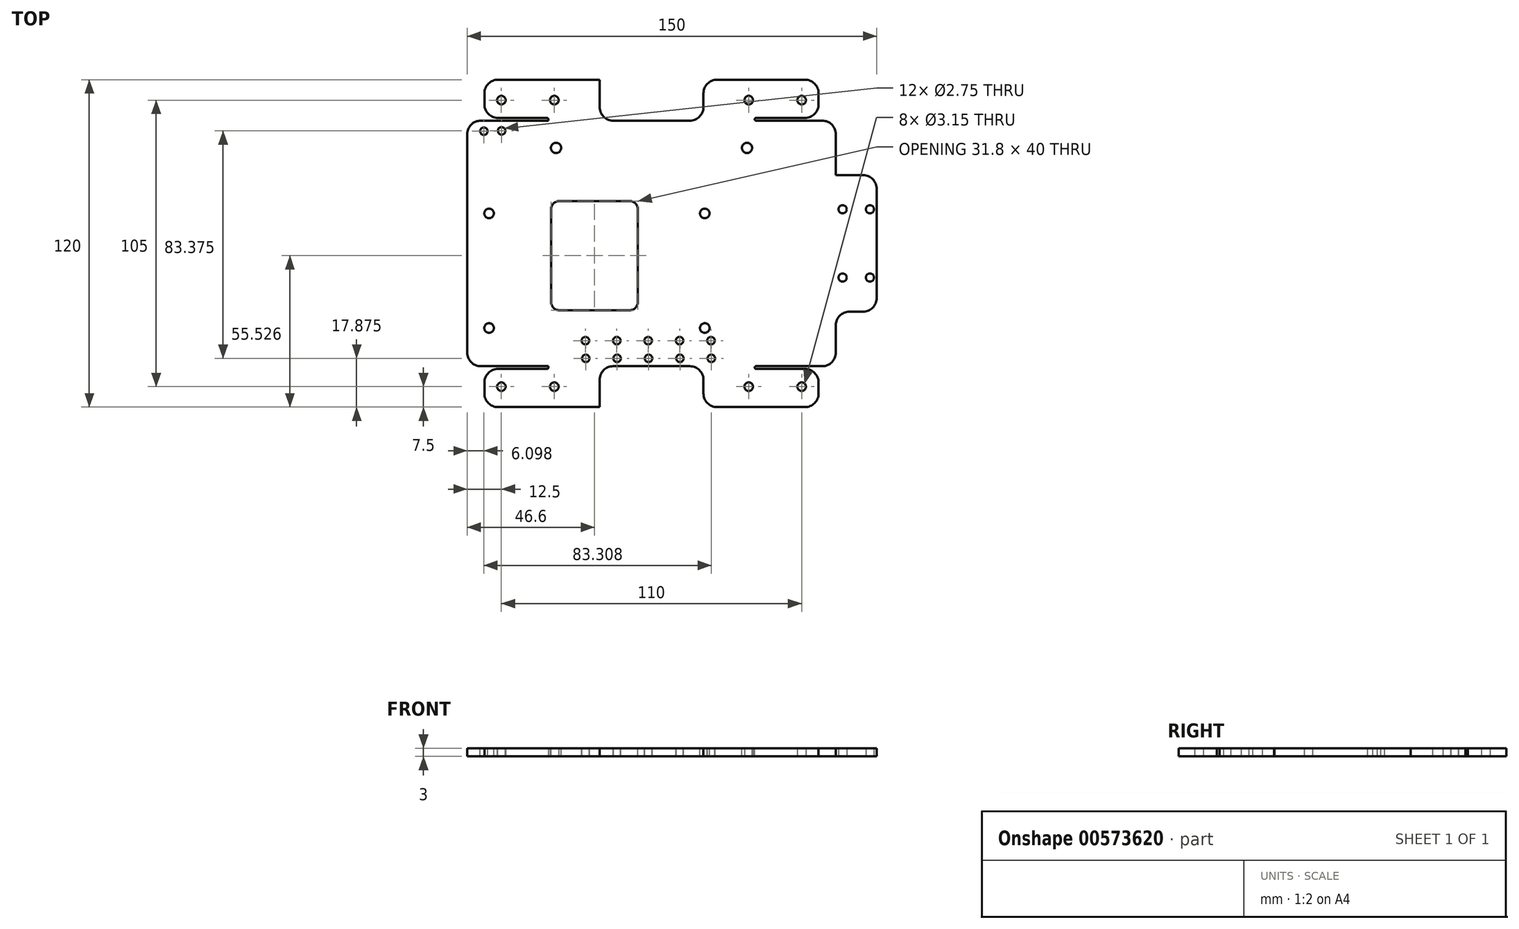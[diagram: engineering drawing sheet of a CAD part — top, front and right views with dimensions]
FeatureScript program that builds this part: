
annotation { "Feature Type Name" : "Feature", "Feature Type Description" : "" }
export const myFeature = defineFeature(function(context is Context, id is Id, definition is map)
    precondition{}
    {
        {
            var Q0;
            Q0=qCreatedBy(makeId("Top.planeOp"),FACE);
            var sketch = newSketch(context, id + "F0", { "sketchPlane" : qUnion([Q0])});
            skLineSegment(sketch, "E0.bottom", {"start": v(67.5, -45) * mm, "end": v(-67.5, -45) * mm});
            skLineSegment(sketch, "E0.top", {"start": v(67.5, 45) * mm, "end": v(-67.5, 45) * mm});
            skLineSegment(sketch, "E0.left", {"start": v(67.5, -45) * mm, "end": v(67.5, 45) * mm});
            skLineSegment(sketch, "E0.right", {"start": v(-67.5, -45) * mm, "end": v(-67.5, 45) * mm});
            skPoint(sketch, "E0.middle", {"position": v(0, 0) * mm});
            skSolve(sketch);
        }
        {
            var Q0;
            Q0 = qSketchRegion(id + "F0", true);
            extrude(context, id + "F1", {"entities" : qUnion([Q0]), "depth" : 3 * mm, "offsetDistance" : 25 * mm});
        }
        {
            var Q0;
            Q0=makeQuery(id+"F1.opExtrude","CAP_FACE",FACE,{"disambiguationData":[OSD([sQuery(id+"F0.wireOp",EDGE,"E0.bottom"),sQuery(id+"F0.wireOp",EDGE,"E0.top"),sQuery(id+"F0.wireOp",EDGE,"E0.left"),sQuery(id+"F0.wireOp",EDGE,"E0.right")])],"isStart":false});
            var sketch = newSketch(context, id + "F2", { "sketchPlane" : qUnion([Q0])});
            skLineSegment(sketch, "E1.bottom", {"start": v(-50.8, 45) * mm, "end": v(-37.8, 45) * mm});
            skLineSegment(sketch, "E1.top", {"start": v(-50.8, -45) * mm, "end": v(-37.8, -45) * mm});
            skLineSegment(sketch, "E1.left", {"start": v(-50.8, 45) * mm, "end": v(-50.8, -45) * mm});
            skLineSegment(sketch, "E1.right", {"start": v(-37.8, 45) * mm, "end": v(-37.8, -45) * mm});
            skLineSegment(sketch, "E2.bottom", {"start": v(37.8, 45) * mm, "end": v(50.8, 45) * mm});
            skLineSegment(sketch, "E2.top", {"start": v(37.8, -45) * mm, "end": v(50.8, -45) * mm});
            skLineSegment(sketch, "E2.left", {"start": v(37.8, 45) * mm, "end": v(37.8, -45) * mm});
            skLineSegment(sketch, "E2.right", {"start": v(50.8, 45) * mm, "end": v(50.8, -45) * mm});
            skLineSegment(sketch, "E3", {"start": v(-37.8, -35.2) * mm, "end": v(37.8, -35.2) * mm, "construction": true});
            skPoint(sketch, "E4", {"position": v(0, -35.2) * mm});
            skLineSegment(sketch, "E5", {"start": v(0, 50.5) * mm, "end": v(0, -49.91) * mm, "construction": true});
            skSolve(sketch);
        }
        {
            var Q0;
            Q0=makeQuery(id+"F1.opExtrude","CAP_FACE",FACE,{"disambiguationData":[OSD([sQuery(id+"F0.wireOp",EDGE,"E0.bottom"),sQuery(id+"F0.wireOp",EDGE,"E0.top"),sQuery(id+"F0.wireOp",EDGE,"E0.left"),sQuery(id+"F0.wireOp",EDGE,"E0.right")])],"isStart":false});
            var sketch = newSketch(context, id + "F3", { "sketchPlane" : qUnion([Q0])});
            skLineSegment(sketch, "E6.bottom", {"start": v(-59.5, 11) * mm, "end": v(19.5, 11) * mm, "construction": true});
            skLineSegment(sketch, "E6.top", {"start": v(-59.5, -31) * mm, "end": v(19.5, -31) * mm, "construction": true});
            skLineSegment(sketch, "E6.left", {"start": v(-59.5, 11) * mm, "end": v(-59.5, -31) * mm, "construction": true});
            skLineSegment(sketch, "E6.right", {"start": v(19.5, 11) * mm, "end": v(19.5, -31) * mm, "construction": true});
            skCircle(sketch, "E7", {"center": v(-59.5, 11) * mm, "radius": 1.75 * mm});
            skCircle(sketch, "E8", {"center": v(19.5, 11) * mm, "radius": 1.75 * mm});
            skCircle(sketch, "E9", {"center": v(19.5, -31) * mm, "radius": 1.75 * mm});
            skCircle(sketch, "E10", {"center": v(-59.5, -31) * mm, "radius": 1.75 * mm});
            skLineSegment(sketch, "E11", {"start": v(-20, 11) * mm, "end": v(-20, -31) * mm, "construction": true});
            skSolve(sketch);
        }
        {
            var Q0;
            Q0 = qSketchRegion(id + "F3", true);
            extrude(context, id + "F4", {"entities" : qUnion([Q0]), "operationType" : NewBodyOperationType.REMOVE, "endBound" : BoundingType.THROUGH_ALL, "oppositeDirection" : true, "depth" : 25 * mm, "offsetDistance" : 25 * mm});
        }
        {
            var Q0;
            Q0=qCreatedBy(makeId("Top.planeOp"),FACE);
            var sketch = newSketch(context, id + "F5", { "sketchPlane" : qUnion([Q0])});
            skLineSegment(sketch, "E12.bottom", {"start": v(-37.8, 45) * mm, "end": v(37.8, 45) * mm});
            skLineSegment(sketch, "E12.top", {"start": v(-37.8, 60) * mm, "end": v(37.8, 60) * mm});
            skLineSegment(sketch, "E12.left", {"start": v(-37.8, 45) * mm, "end": v(-37.8, 46) * mm});
            skLineSegment(sketch, "E12.right", {"start": v(37.8, 45) * mm, "end": v(37.8, 46) * mm});
            skLineSegment(sketch, "E13", {"start": v(0, 42.7) * mm, "end": v(0, -42.57) * mm, "construction": true});
            skLineSegment(sketch, "E14", {"start": v(-65.02, 0) * mm, "end": v(65.15, 0) * mm, "construction": true});
            skCircle(sketch, "E15", {"center": v(-55, 52.5) * mm, "radius": 1.57 * mm});
            skCircle(sketch, "E16", {"center": v(-35.6, 52.5) * mm, "radius": 1.57 * mm});
            skLineSegment(sketch, "E17", {"start": v(-55, 52.5) * mm, "end": v(-35.6, 52.5) * mm, "construction": true});
            skLineSegment(sketch, "E18", {"start": v(-45.3, 60) * mm, "end": v(-45.3, 45) * mm, "construction": true});
            skPoint(sketch, "E19", {"position": v(-45.3, 52.5) * mm});
            skPoint(sketch, "E19.positionSnap0", {"position": v(-45.3, 52.5) * mm});
            skCircle(sketch, "E20", {"center": v(-55, 52.5) * mm, "radius": 2.2 * mm, "construction": true});
            skCircle(sketch, "E21", {"center": v(-35.6, 52.5) * mm, "radius": 2.2 * mm, "construction": true});
            skLineSegment(sketch, "E22.bottom", {"start": v(-37.8, 46) * mm, "end": v(-61.2, 46) * mm});
            skLineSegment(sketch, "E22.top", {"start": v(-37.76, 60) * mm, "end": v(-61.2, 60) * mm});
            skLineSegment(sketch, "E22.right", {"start": v(-61.2, 46) * mm, "end": v(-61.2, 60) * mm});
            skPoint(sketch, "E23.MirrorP", {"position": v(45.3, 52.5) * mm});
            skLineSegment(sketch, "E24.MirrorCS", {"start": v(55, 52.5) * mm, "end": v(35.6, 52.5) * mm, "construction": true});
            skLineSegment(sketch, "E25.MirrorCS", {"start": v(45.3, 60) * mm, "end": v(45.3, 45) * mm, "construction": true});
            skCircle(sketch, "E26.MirrorC", {"center": v(55, 52.5) * mm, "radius": 2.2 * mm, "construction": true});
            skCircle(sketch, "E27.MirrorC", {"center": v(55, 52.5) * mm, "radius": 1.57 * mm});
            skCircle(sketch, "E28.MirrorC", {"center": v(35.6, 52.5) * mm, "radius": 1.57 * mm});
            skCircle(sketch, "E29.MirrorC", {"center": v(35.6, 52.5) * mm, "radius": 2.2 * mm, "construction": true});
            skLineSegment(sketch, "E30.bottom", {"start": v(37.8, 60) * mm, "end": v(61.2, 60) * mm});
            skLineSegment(sketch, "E30.top", {"start": v(37.8, 46) * mm, "end": v(61.2, 46) * mm});
            skLineSegment(sketch, "E30.right", {"start": v(61.2, 60) * mm, "end": v(61.2, 46) * mm});
            skLineSegment(sketch, "E31", {"start": v(-57.2, 52.5) * mm, "end": v(-61.2, 52.5) * mm, "construction": true});
            skLineSegment(sketch, "E32", {"start": v(57.2, 52.5) * mm, "end": v(61.2, 52.5) * mm, "construction": true});
            skLineSegment(sketch, "E33.MirrorCS", {"start": v(37.8, -45) * mm, "end": v(37.8, -46) * mm});
            skLineSegment(sketch, "E34.MirrorCS", {"start": v(-37.8, -45) * mm, "end": v(-37.8, -46) * mm});
            skPoint(sketch, "E35.MirrorP", {"position": v(-45.3, -52.5) * mm});
            skPoint(sketch, "E36.MirrorP", {"position": v(45.3, -52.5) * mm});
            skLineSegment(sketch, "E37.MirrorCS", {"start": v(-57.2, -52.5) * mm, "end": v(-61.2, -52.5) * mm, "construction": true});
            skCircle(sketch, "E38.MirrorC", {"center": v(-35.6, -52.5) * mm, "radius": 2.2 * mm, "construction": true});
            skLineSegment(sketch, "E39.MirrorCS", {"start": v(61.2, -60) * mm, "end": v(61.2, -46) * mm});
            skLineSegment(sketch, "E40.MirrorCS", {"start": v(45.3, -60) * mm, "end": v(45.3, -45) * mm, "construction": true});
            skLineSegment(sketch, "E41.MirrorCS", {"start": v(57.2, -52.5) * mm, "end": v(61.2, -52.5) * mm, "construction": true});
            skCircle(sketch, "E42.MirrorC", {"center": v(-55, -52.5) * mm, "radius": 2.2 * mm, "construction": true});
            skCircle(sketch, "E43.MirrorC", {"center": v(55, -52.5) * mm, "radius": 1.57 * mm});
            skLineSegment(sketch, "E44.MirrorCS", {"start": v(55, -52.5) * mm, "end": v(35.6, -52.5) * mm, "construction": true});
            skLineSegment(sketch, "E45.MirrorCS", {"start": v(-55, -52.5) * mm, "end": v(-35.6, -52.5) * mm, "construction": true});
            skLineSegment(sketch, "E46.MirrorCS", {"start": v(-45.3, -60) * mm, "end": v(-45.3, -45) * mm, "construction": true});
            skCircle(sketch, "E47.MirrorC", {"center": v(35.6, -52.5) * mm, "radius": 1.57 * mm});
            skLineSegment(sketch, "E48.MirrorCS", {"start": v(37.8, -46) * mm, "end": v(61.2, -46) * mm});
            skCircle(sketch, "E49.MirrorC", {"center": v(-35.6, -52.5) * mm, "radius": 1.57 * mm});
            skLineSegment(sketch, "E50.MirrorCS", {"start": v(37.8, -60) * mm, "end": v(61.2, -60) * mm});
            skLineSegment(sketch, "E51.MirrorCS", {"start": v(-37.8, -45) * mm, "end": v(37.8, -45) * mm});
            skCircle(sketch, "E52.MirrorC", {"center": v(55, -52.5) * mm, "radius": 2.2 * mm, "construction": true});
            skLineSegment(sketch, "E53.MirrorCS", {"start": v(-61.2, -46) * mm, "end": v(-61.2, -60) * mm});
            skCircle(sketch, "E54.MirrorC", {"center": v(-55, -52.5) * mm, "radius": 1.57 * mm});
            skLineSegment(sketch, "E55.MirrorCS", {"start": v(-37.76, -60) * mm, "end": v(-61.2, -60) * mm});
            skLineSegment(sketch, "E56.MirrorCS", {"start": v(-37.8, -60) * mm, "end": v(37.8, -60) * mm});
            skCircle(sketch, "E57.MirrorC", {"center": v(35.6, -52.5) * mm, "radius": 2.2 * mm, "construction": true});
            skLineSegment(sketch, "E58.MirrorCS", {"start": v(-37.8, -46) * mm, "end": v(-61.2, -46) * mm});
            skSolve(sketch);
        }
        {
            var Q0;
            Q0 = qSketchRegion(id + "F5", true);
            var Q1;
            Q1=makeQuery(id+"F1.opExtrude","CAP_FACE",FACE,{"disambiguationData":[OSD([sQuery(id+"F0.wireOp",EDGE,"E0.bottom"),sQuery(id+"F0.wireOp",EDGE,"E0.top"),sQuery(id+"F0.wireOp",EDGE,"E0.left"),sQuery(id+"F0.wireOp",EDGE,"E0.right")])],"isStart":false});
            extrude(context, id + "F6", {"entities" : qUnion([Q0]), "operationType" : NewBodyOperationType.ADD, "endBound" : BoundingType.UP_TO_SURFACE, "depth" : 25 * mm, "endBoundEntityFace" : qUnion([Q1]), "offsetDistance" : 25 * mm});
        }
        {
            var Q0;
            {var subQ0=sQuery(id+"F0.wireOp",EDGE,"E0.right");var subQ1=sQuery(id+"F0.wireOp",EDGE,"E0.left");var subQ2=sQuery(id+"F0.wireOp",EDGE,"E0.top");var subQ3=sQuery(id+"F0.wireOp",EDGE,"E0.bottom");Q0=makeQuery(id+"F6.boolean.opBoolean","MERGE",FACE,{"derivedFrom":[makeQuery(id+"F1.opExtrude","CAP_FACE",FACE,{"disambiguationData":[OSD([subQ3,subQ2,subQ1,subQ0])],"isStart":false}),makeQuery(id+"F6.opExtrude","CAP_FACE",FACE,{"disambiguationData":[OSD([subQ3,subQ2,subQ1,subQ0]),OD(0.0)],"isStart":false}),makeQuery(id+"F6.opExtrude","CAP_FACE",FACE,{"disambiguationData":[OSD([subQ3,subQ2,subQ1,subQ0]),OD(1.0)],"isStart":false})]});}
            var sketch = newSketch(context, id + "F7", { "sketchPlane" : qUnion([Q0])});
            skLineSegment(sketch, "E59.bottom", {"start": v(-19.02, -60) * mm, "end": v(19.02, -60) * mm});
            skLineSegment(sketch, "E59.top", {"start": v(-19.02, -45) * mm, "end": v(19.02, -45) * mm});
            skLineSegment(sketch, "E59.left", {"start": v(-19.02, -60) * mm, "end": v(-19.02, -45) * mm});
            skLineSegment(sketch, "E59.right", {"start": v(19.02, -60) * mm, "end": v(19.02, -45) * mm});
            skLineSegment(sketch, "E60", {"start": v(0, -60) * mm, "end": v(0, -45) * mm, "construction": true});
            skLineSegment(sketch, "E61", {"start": v(-67.5, 0) * mm, "end": v(67.5, 0) * mm, "construction": true});
            skLineSegment(sketch, "E62.MirrorCS", {"start": v(-19.02, 45) * mm, "end": v(19.02, 45) * mm});
            skLineSegment(sketch, "E63.MirrorCS", {"start": v(-19.02, 60) * mm, "end": v(19.02, 60) * mm});
            skLineSegment(sketch, "E64.MirrorCS", {"start": v(19.02, 60) * mm, "end": v(19.02, 45) * mm});
            skLineSegment(sketch, "E65.MirrorCS", {"start": v(-19.02, 60) * mm, "end": v(-19.02, 45) * mm});
            skSolve(sketch);
        }
        {
            var Q0;
            Q0 = qSketchRegion(id + "F7", true);
            var Q1;
            Q1=makeQuery(id+"F6.boolean.opBoolean","MERGE",FACE,{"derivedFrom":[makeQuery(id+"F1.opExtrude","CAP_FACE",FACE,{"disambiguationData":[OSD([sQuery(id+"F0.wireOp",EDGE,"E0.bottom"),sQuery(id+"F0.wireOp",EDGE,"E0.top"),sQuery(id+"F0.wireOp",EDGE,"E0.left"),sQuery(id+"F0.wireOp",EDGE,"E0.right")])],"isStart":true}),makeQuery(id+"F6.opExtrude","CAP_FACE",FACE,{"disambiguationData":[OSD([sQuery(id+"F5.wireOp",EDGE,"E12.bottom"),sQuery(id+"F5.wireOp",EDGE,"E12.top"),sQuery(id+"F5.wireOp",EDGE,"E12.left"),sQuery(id+"F5.wireOp",EDGE,"E15"),sQuery(id+"F5.wireOp",EDGE,"E16"),sQuery(id+"F5.wireOp",EDGE,"E22.bottom"),sQuery(id+"F5.wireOp",EDGE,"E22.top"),sQuery(id+"F5.wireOp",EDGE,"E22.right"),sQuery(id+"F5.wireOp",EDGE,"E12.right"),sQuery(id+"F5.wireOp",EDGE,"E27.MirrorC"),sQuery(id+"F5.wireOp",EDGE,"E28.MirrorC"),sQuery(id+"F5.wireOp",EDGE,"E30.bottom"),sQuery(id+"F5.wireOp",EDGE,"E30.top"),sQuery(id+"F5.wireOp",EDGE,"E30.right")])],"isStart":true}),makeQuery(id+"F6.opExtrude","CAP_FACE",FACE,{"disambiguationData":[OSD([sQuery(id+"F5.wireOp",EDGE,"E33.MirrorCS"),sQuery(id+"F5.wireOp",EDGE,"E34.MirrorCS"),sQuery(id+"F5.wireOp",EDGE,"E39.MirrorCS"),sQuery(id+"F5.wireOp",EDGE,"E43.MirrorC"),sQuery(id+"F5.wireOp",EDGE,"E47.MirrorC"),sQuery(id+"F5.wireOp",EDGE,"E48.MirrorCS"),sQuery(id+"F5.wireOp",EDGE,"E49.MirrorC"),sQuery(id+"F5.wireOp",EDGE,"E50.MirrorCS"),sQuery(id+"F5.wireOp",EDGE,"E51.MirrorCS"),sQuery(id+"F5.wireOp",EDGE,"E53.MirrorCS"),sQuery(id+"F5.wireOp",EDGE,"E54.MirrorC"),sQuery(id+"F5.wireOp",EDGE,"E55.MirrorCS"),sQuery(id+"F5.wireOp",EDGE,"E56.MirrorCS"),sQuery(id+"F5.wireOp",EDGE,"E58.MirrorCS")])],"isStart":true})]});
            extrude(context, id + "F8", {"entities" : qUnion([Q0]), "operationType" : NewBodyOperationType.REMOVE, "endBound" : BoundingType.UP_TO_SURFACE, "oppositeDirection" : true, "depth" : 25 * mm, "endBoundEntityFace" : qUnion([Q1]), "offsetDistance" : 25 * mm});
        }
        {
            var Q0;
            {var subQ0=sQuery(id+"F0.wireOp",EDGE,"E0.right");var subQ1=sQuery(id+"F0.wireOp",EDGE,"E0.left");var subQ2=sQuery(id+"F0.wireOp",EDGE,"E0.top");var subQ3=sQuery(id+"F0.wireOp",EDGE,"E0.bottom");Q0=makeQuery(id+"F6.boolean.opBoolean","MERGE",FACE,{"derivedFrom":[makeQuery(id+"F1.opExtrude","CAP_FACE",FACE,{"disambiguationData":[OSD([subQ3,subQ2,subQ1,subQ0])],"isStart":false}),makeQuery(id+"F6.opExtrude","CAP_FACE",FACE,{"disambiguationData":[OSD([subQ3,subQ2,subQ1,subQ0]),OD(0.0)],"isStart":false}),makeQuery(id+"F6.opExtrude","CAP_FACE",FACE,{"disambiguationData":[OSD([subQ3,subQ2,subQ1,subQ0]),OD(1.0)],"isStart":false})]});}
            var sketch = newSketch(context, id + "F9", { "sketchPlane" : qUnion([Q0])});
            skCircle(sketch, "E66", {"center": v(-61.4, 41.12) * mm, "radius": 1.38 * mm});
            skCircle(sketch, "E67", {"center": v(-54.9, 41.25) * mm, "radius": 1.38 * mm});
            skLineSegment(sketch, "E68", {"start": v(-61.4, 41.12) * mm, "end": v(-54.9, 41.25) * mm, "construction": true});
            skCircle(sketch, "E69", {"center": v(-24.22, -35.63) * mm, "radius": 1.38 * mm});
            skCircle(sketch, "E70", {"center": v(-24.1, -42.12) * mm, "radius": 1.38 * mm});
            skLineSegment(sketch, "E71", {"start": v(-24.22, -35.63) * mm, "end": v(-24.1, -42.13) * mm, "construction": true});
            skLineSegment(sketch, "E72.1.0.0", {"start": v(-12.72, -35.63) * mm, "end": v(-12.6, -42.12) * mm, "construction": true});
            skCircle(sketch, "E72.1.0.1", {"center": v(-12.6, -42.12) * mm, "radius": 1.38 * mm});
            skCircle(sketch, "E72.1.0.2", {"center": v(-12.72, -35.63) * mm, "radius": 1.38 * mm});
            skCircle(sketch, "E72.1.0.3", {"center": v(-12.72, -35.63) * mm, "radius": 1.38 * mm});
            skCircle(sketch, "E72.1.0.4", {"center": v(-12.6, -42.12) * mm, "radius": 1.38 * mm});
            skLineSegment(sketch, "E72.2.0.0", {"start": v(-1.22, -35.63) * mm, "end": v(-1.1, -42.13) * mm, "construction": true});
            skCircle(sketch, "E72.2.0.1", {"center": v(-1.1, -42.12) * mm, "radius": 1.38 * mm});
            skCircle(sketch, "E72.2.0.2", {"center": v(-1.22, -35.63) * mm, "radius": 1.38 * mm});
            skCircle(sketch, "E72.2.0.3", {"center": v(-1.22, -35.63) * mm, "radius": 1.38 * mm});
            skCircle(sketch, "E72.2.0.4", {"center": v(-1.1, -42.12) * mm, "radius": 1.38 * mm});
            skLineSegment(sketch, "E72.direction1", {"start": v(-24.1, -42.13) * mm, "end": v(-12.6, -42.13) * mm, "construction": true});
            skLineSegment(sketch, "E73.0.3.0", {"start": v(10.28, -35.63) * mm, "end": v(10.4, -42.13) * mm, "construction": true});
            skCircle(sketch, "E73.3.3.0", {"center": v(10.4, -42.12) * mm, "radius": 1.38 * mm});
            skCircle(sketch, "E73.5.3.0", {"center": v(10.28, -35.63) * mm, "radius": 1.38 * mm});
            skCircle(sketch, "E73.7.3.0", {"center": v(10.28, -35.63) * mm, "radius": 1.38 * mm});
            skCircle(sketch, "E73.9.3.0", {"center": v(10.4, -42.12) * mm, "radius": 1.38 * mm});
            skLineSegment(sketch, "E73.0.4.0", {"start": v(21.78, -35.63) * mm, "end": v(21.9, -42.13) * mm, "construction": true});
            skCircle(sketch, "E73.3.4.0", {"center": v(21.9, -42.13) * mm, "radius": 1.38 * mm});
            skCircle(sketch, "E73.5.4.0", {"center": v(21.78, -35.63) * mm, "radius": 1.38 * mm});
            skCircle(sketch, "E73.7.4.0", {"center": v(21.78, -35.63) * mm, "radius": 1.38 * mm});
            skCircle(sketch, "E73.9.4.0", {"center": v(21.9, -42.13) * mm, "radius": 1.38 * mm});
            skSolve(sketch);
        }
        {
            var Q0;
            Q0 = qSketchRegion(id + "F9", true);
            var Q1;
            Q1=makeQuery(id+"F6.boolean.opBoolean","MERGE",FACE,{"derivedFrom":[makeQuery(id+"F1.opExtrude","CAP_FACE",FACE,{"disambiguationData":[OSD([sQuery(id+"F0.wireOp",EDGE,"E0.bottom"),sQuery(id+"F0.wireOp",EDGE,"E0.top"),sQuery(id+"F0.wireOp",EDGE,"E0.left"),sQuery(id+"F0.wireOp",EDGE,"E0.right")])],"isStart":true}),makeQuery(id+"F6.opExtrude","CAP_FACE",FACE,{"disambiguationData":[OSD([sQuery(id+"F5.wireOp",EDGE,"E12.bottom"),sQuery(id+"F5.wireOp",EDGE,"E12.top"),sQuery(id+"F5.wireOp",EDGE,"E12.left"),sQuery(id+"F5.wireOp",EDGE,"E15"),sQuery(id+"F5.wireOp",EDGE,"E16"),sQuery(id+"F5.wireOp",EDGE,"E22.bottom"),sQuery(id+"F5.wireOp",EDGE,"E22.top"),sQuery(id+"F5.wireOp",EDGE,"E22.right"),sQuery(id+"F5.wireOp",EDGE,"E12.right"),sQuery(id+"F5.wireOp",EDGE,"E27.MirrorC"),sQuery(id+"F5.wireOp",EDGE,"E28.MirrorC"),sQuery(id+"F5.wireOp",EDGE,"E30.bottom"),sQuery(id+"F5.wireOp",EDGE,"E30.top"),sQuery(id+"F5.wireOp",EDGE,"E30.right")])],"isStart":true}),makeQuery(id+"F6.opExtrude","CAP_FACE",FACE,{"disambiguationData":[OSD([sQuery(id+"F5.wireOp",EDGE,"E33.MirrorCS"),sQuery(id+"F5.wireOp",EDGE,"E34.MirrorCS"),sQuery(id+"F5.wireOp",EDGE,"E39.MirrorCS"),sQuery(id+"F5.wireOp",EDGE,"E43.MirrorC"),sQuery(id+"F5.wireOp",EDGE,"E47.MirrorC"),sQuery(id+"F5.wireOp",EDGE,"E48.MirrorCS"),sQuery(id+"F5.wireOp",EDGE,"E49.MirrorC"),sQuery(id+"F5.wireOp",EDGE,"E50.MirrorCS"),sQuery(id+"F5.wireOp",EDGE,"E51.MirrorCS"),sQuery(id+"F5.wireOp",EDGE,"E53.MirrorCS"),sQuery(id+"F5.wireOp",EDGE,"E54.MirrorC"),sQuery(id+"F5.wireOp",EDGE,"E55.MirrorCS"),sQuery(id+"F5.wireOp",EDGE,"E56.MirrorCS"),sQuery(id+"F5.wireOp",EDGE,"E58.MirrorCS")])],"isStart":true})]});
            extrude(context, id + "F10", {"entities" : qUnion([Q0]), "operationType" : NewBodyOperationType.REMOVE, "endBound" : BoundingType.UP_TO_SURFACE, "oppositeDirection" : true, "depth" : 25 * mm, "endBoundEntityFace" : qUnion([Q1]), "offsetDistance" : 25 * mm});
        }
        {
            var Q0;
            {var subQ0=sQuery(id+"F0.wireOp",EDGE,"E0.right");var subQ1=sQuery(id+"F0.wireOp",EDGE,"E0.left");var subQ2=sQuery(id+"F0.wireOp",EDGE,"E0.top");var subQ3=sQuery(id+"F0.wireOp",EDGE,"E0.bottom");Q0=makeQuery(id+"F6.boolean.opBoolean","MERGE",FACE,{"derivedFrom":[makeQuery(id+"F1.opExtrude","CAP_FACE",FACE,{"disambiguationData":[OSD([subQ3,subQ2,subQ1,subQ0])],"isStart":false}),makeQuery(id+"F6.opExtrude","CAP_FACE",FACE,{"disambiguationData":[OSD([subQ3,subQ2,subQ1,subQ0]),OD(0.0)],"isStart":false}),makeQuery(id+"F6.opExtrude","CAP_FACE",FACE,{"disambiguationData":[OSD([subQ3,subQ2,subQ1,subQ0]),OD(1.0)],"isStart":false})]});}
            var sketch = newSketch(context, id + "F11", { "sketchPlane" : qUnion([Q0])});
            skLineSegment(sketch, "E74.bottom", {"start": v(-36.8, 15.53) * mm, "end": v(-5, 15.53) * mm});
            skLineSegment(sketch, "E74.top", {"start": v(-36.8, -24.47) * mm, "end": v(-5, -24.47) * mm});
            skLineSegment(sketch, "E74.left", {"start": v(-36.8, 15.53) * mm, "end": v(-36.8, -24.47) * mm});
            skLineSegment(sketch, "E74.right", {"start": v(-5, 15.53) * mm, "end": v(-5, -24.47) * mm});
            skLineSegment(sketch, "E75", {"start": v(-67.5, 0) * mm, "end": v(67.5, 0) * mm, "construction": true});
            skSolve(sketch);
        }
        {
            var Q0;
            Q0 = qSketchRegion(id + "F11", true);
            var Q1;
            Q1=makeQuery(id+"F6.boolean.opBoolean","MERGE",FACE,{"derivedFrom":[makeQuery(id+"F1.opExtrude","CAP_FACE",FACE,{"disambiguationData":[OSD([sQuery(id+"F0.wireOp",EDGE,"E0.bottom"),sQuery(id+"F0.wireOp",EDGE,"E0.top"),sQuery(id+"F0.wireOp",EDGE,"E0.left"),sQuery(id+"F0.wireOp",EDGE,"E0.right")])],"isStart":true}),makeQuery(id+"F6.opExtrude","CAP_FACE",FACE,{"disambiguationData":[OSD([sQuery(id+"F5.wireOp",EDGE,"E12.bottom"),sQuery(id+"F5.wireOp",EDGE,"E12.top"),sQuery(id+"F5.wireOp",EDGE,"E12.left"),sQuery(id+"F5.wireOp",EDGE,"E15"),sQuery(id+"F5.wireOp",EDGE,"E16"),sQuery(id+"F5.wireOp",EDGE,"E22.bottom"),sQuery(id+"F5.wireOp",EDGE,"E22.top"),sQuery(id+"F5.wireOp",EDGE,"E22.right"),sQuery(id+"F5.wireOp",EDGE,"E12.right"),sQuery(id+"F5.wireOp",EDGE,"E27.MirrorC"),sQuery(id+"F5.wireOp",EDGE,"E28.MirrorC"),sQuery(id+"F5.wireOp",EDGE,"E30.bottom"),sQuery(id+"F5.wireOp",EDGE,"E30.top"),sQuery(id+"F5.wireOp",EDGE,"E30.right")])],"isStart":true}),makeQuery(id+"F6.opExtrude","CAP_FACE",FACE,{"disambiguationData":[OSD([sQuery(id+"F5.wireOp",EDGE,"E33.MirrorCS"),sQuery(id+"F5.wireOp",EDGE,"E34.MirrorCS"),sQuery(id+"F5.wireOp",EDGE,"E39.MirrorCS"),sQuery(id+"F5.wireOp",EDGE,"E43.MirrorC"),sQuery(id+"F5.wireOp",EDGE,"E47.MirrorC"),sQuery(id+"F5.wireOp",EDGE,"E48.MirrorCS"),sQuery(id+"F5.wireOp",EDGE,"E49.MirrorC"),sQuery(id+"F5.wireOp",EDGE,"E50.MirrorCS"),sQuery(id+"F5.wireOp",EDGE,"E51.MirrorCS"),sQuery(id+"F5.wireOp",EDGE,"E53.MirrorCS"),sQuery(id+"F5.wireOp",EDGE,"E54.MirrorC"),sQuery(id+"F5.wireOp",EDGE,"E55.MirrorCS"),sQuery(id+"F5.wireOp",EDGE,"E56.MirrorCS"),sQuery(id+"F5.wireOp",EDGE,"E58.MirrorCS")])],"isStart":true})]});
            extrude(context, id + "F12", {"entities" : qUnion([Q0]), "operationType" : NewBodyOperationType.REMOVE, "endBound" : BoundingType.UP_TO_SURFACE, "oppositeDirection" : true, "depth" : 25 * mm, "endBoundEntityFace" : qUnion([Q1]), "offsetDistance" : 25 * mm});
        }
        {
            var Q0;
            Q0=qCreatedBy(makeId("Top.planeOp"),FACE);
            var sketch = newSketch(context, id + "F13", { "sketchPlane" : qUnion([Q0])});
            skLineSegment(sketch, "E76.bottom", {"start": v(67.5, 25) * mm, "end": v(82.5, 25) * mm});
            skLineSegment(sketch, "E76.top", {"start": v(67.5, -25) * mm, "end": v(82.5, -25) * mm});
            skLineSegment(sketch, "E76.left", {"start": v(67.5, 25) * mm, "end": v(67.5, -25) * mm});
            skLineSegment(sketch, "E76.right", {"start": v(82.5, 25) * mm, "end": v(82.5, -25) * mm});
            skLineSegment(sketch, "E77", {"start": v(82.5, 0) * mm, "end": v(67.5, 0) * mm, "construction": true});
            skCircle(sketch, "E78", {"center": v(70, 12.5) * mm, "radius": 1.5 * mm});
            skLineSegment(sketch, "E79", {"start": v(75, 25) * mm, "end": v(75, -25) * mm, "construction": true});
            skCircle(sketch, "E80.MirrorC", {"center": v(80, 12.5) * mm, "radius": 1.5 * mm});
            skCircle(sketch, "E81.MirrorC", {"center": v(80, -12.5) * mm, "radius": 1.5 * mm});
            skCircle(sketch, "E82.MirrorC", {"center": v(70, -12.5) * mm, "radius": 1.5 * mm});
            skSolve(sketch);
        }
        {
            var Q0;
            Q0 = qSketchRegion(id + "F13", true);
            var Q1;
            {var subQ0=sQuery(id+"F0.wireOp",EDGE,"E0.right");var subQ1=sQuery(id+"F0.wireOp",EDGE,"E0.left");var subQ2=sQuery(id+"F0.wireOp",EDGE,"E0.top");var subQ3=sQuery(id+"F0.wireOp",EDGE,"E0.bottom");Q1=makeQuery(id+"F6.boolean.opBoolean","MERGE",FACE,{"derivedFrom":[makeQuery(id+"F1.opExtrude","CAP_FACE",FACE,{"disambiguationData":[OSD([subQ3,subQ2,subQ1,subQ0])],"isStart":false}),makeQuery(id+"F6.opExtrude","CAP_FACE",FACE,{"disambiguationData":[OSD([subQ3,subQ2,subQ1,subQ0]),OD(0.0)],"isStart":false}),makeQuery(id+"F6.opExtrude","CAP_FACE",FACE,{"disambiguationData":[OSD([subQ3,subQ2,subQ1,subQ0]),OD(1.0)],"isStart":false})]});}
            extrude(context, id + "F14", {"entities" : qUnion([Q0]), "operationType" : NewBodyOperationType.ADD, "endBound" : BoundingType.UP_TO_SURFACE, "depth" : 25 * mm, "endBoundEntityFace" : qUnion([Q1]), "offsetDistance" : 25 * mm});
        }
        {
            var Q0;
            Q0=makeQuery(id+"F12.boolean.opBoolean","COPY",EDGE,{"derivedFrom":makeQuery(id+"F12.opExtrude","SWEPT_EDGE",EDGE,{"disambiguationData":[OSD([sQuery(id+"F11.wireOp",EDGE,"xUbogBU6-eH2m-k65I-W5yT-uLPt3hoXtkAA.bottom"),sQuery(id+"F11.wireOp",EDGE,"xUbogBU6-eH2m-k65I-W5yT-uLPt3hoXtkAA.left")])]})});
            var Q1;
            Q1=makeQuery(id+"F12.boolean.opBoolean","COPY",EDGE,{"derivedFrom":makeQuery(id+"F12.opExtrude","SWEPT_EDGE",EDGE,{"disambiguationData":[OSD([sQuery(id+"F11.wireOp",EDGE,"xUbogBU6-eH2m-k65I-W5yT-uLPt3hoXtkAA.bottom"),sQuery(id+"F11.wireOp",EDGE,"xUbogBU6-eH2m-k65I-W5yT-uLPt3hoXtkAA.right")])]})});
            var Q2;
            Q2=makeQuery(id+"F12.boolean.opBoolean","COPY",EDGE,{"derivedFrom":makeQuery(id+"F12.opExtrude","SWEPT_EDGE",EDGE,{"disambiguationData":[OSD([sQuery(id+"F11.wireOp",EDGE,"xUbogBU6-eH2m-k65I-W5yT-uLPt3hoXtkAA.top"),sQuery(id+"F11.wireOp",EDGE,"xUbogBU6-eH2m-k65I-W5yT-uLPt3hoXtkAA.right")])]})});
            var Q3;
            Q3=makeQuery(id+"F12.boolean.opBoolean","COPY",EDGE,{"derivedFrom":makeQuery(id+"F12.opExtrude","SWEPT_EDGE",EDGE,{"disambiguationData":[OSD([sQuery(id+"F11.wireOp",EDGE,"xUbogBU6-eH2m-k65I-W5yT-uLPt3hoXtkAA.top"),sQuery(id+"F11.wireOp",EDGE,"xUbogBU6-eH2m-k65I-W5yT-uLPt3hoXtkAA.left")])]})});
            var Q4;
            Q4=makeQuery(id+"F12.boolean.opBoolean","COPY",EDGE,{"derivedFrom":makeQuery(id+"F12.opExtrude","SWEPT_EDGE",EDGE,{"disambiguationData":[OSD([sQuery(id+"F11.wireOp",EDGE,"E74.top"),sQuery(id+"F11.wireOp",EDGE,"E74.left")])]})});
            var Q5;
            Q5=makeQuery(id+"F12.boolean.opBoolean","COPY",EDGE,{"derivedFrom":makeQuery(id+"F12.opExtrude","SWEPT_EDGE",EDGE,{"disambiguationData":[OSD([sQuery(id+"F11.wireOp",EDGE,"E74.top"),sQuery(id+"F11.wireOp",EDGE,"E74.right")])]})});
            var Q6;
            Q6=makeQuery(id+"F12.boolean.opBoolean","COPY",EDGE,{"derivedFrom":makeQuery(id+"F12.opExtrude","SWEPT_EDGE",EDGE,{"disambiguationData":[OSD([sQuery(id+"F11.wireOp",EDGE,"E74.bottom"),sQuery(id+"F11.wireOp",EDGE,"E74.right")])]})});
            var Q7;
            Q7=makeQuery(id+"F12.boolean.opBoolean","COPY",EDGE,{"derivedFrom":makeQuery(id+"F12.opExtrude","SWEPT_EDGE",EDGE,{"disambiguationData":[OSD([sQuery(id+"F11.wireOp",EDGE,"E74.bottom"),sQuery(id+"F11.wireOp",EDGE,"E74.left")])]})});
            fillet(context, id + "F15", {"entities" : qUnion([Q0, Q1, Q2, Q3, Q4, Q5, Q6, Q7]), "radius" : 3 * mm, "tangentPropagation" : true, "allowEdgeOverflow" : false});
        }
        {
            var Q0;
            Q0=makeQuery(id+"F6.opExtrude","SWEPT_EDGE",EDGE,{"disambiguationData":[OSD([sQuery(id+"F5.wireOp",EDGE,"E12.left"),sQuery(id+"F5.wireOp",EDGE,"E22.bottom")])]});
            var Q1;
            Q1=makeQuery(id+"F6.opExtrude","SWEPT_EDGE",EDGE,{"disambiguationData":[OSD([sQuery(id+"F5.wireOp",EDGE,"E12.bottom"),sQuery(id+"F5.wireOp",EDGE,"E12.left")])]});
            var Q2;
            Q2=makeQuery(id+"F6.opExtrude","SWEPT_EDGE",EDGE,{"disambiguationData":[OSD([sQuery(id+"F5.wireOp",EDGE,"E12.right"),sQuery(id+"F5.wireOp",EDGE,"E30.top")])]});
            var Q3;
            Q3=makeQuery(id+"F6.opExtrude","SWEPT_EDGE",EDGE,{"disambiguationData":[OSD([sQuery(id+"F5.wireOp",EDGE,"E12.bottom"),sQuery(id+"F5.wireOp",EDGE,"E12.right")])]});
            var Q4;
            Q4=makeQuery(id+"F6.opExtrude","SWEPT_EDGE",EDGE,{"disambiguationData":[OSD([sQuery(id+"F5.wireOp",EDGE,"E33.MirrorCS"),sQuery(id+"F5.wireOp",EDGE,"E51.MirrorCS")])]});
            var Q5;
            Q5=makeQuery(id+"F6.opExtrude","SWEPT_EDGE",EDGE,{"disambiguationData":[OSD([sQuery(id+"F5.wireOp",EDGE,"E33.MirrorCS"),sQuery(id+"F5.wireOp",EDGE,"E48.MirrorCS")])]});
            var Q6;
            Q6=makeQuery(id+"F6.opExtrude","SWEPT_EDGE",EDGE,{"disambiguationData":[OSD([sQuery(id+"F5.wireOp",EDGE,"E34.MirrorCS"),sQuery(id+"F5.wireOp",EDGE,"E58.MirrorCS")])]});
            var Q7;
            Q7=makeQuery(id+"F6.opExtrude","SWEPT_EDGE",EDGE,{"disambiguationData":[OSD([sQuery(id+"F5.wireOp",EDGE,"E34.MirrorCS"),sQuery(id+"F5.wireOp",EDGE,"E51.MirrorCS")])]});
            fillet(context, id + "F16", {"entities" : qUnion([Q0, Q1, Q2, Q3, Q4, Q5, Q6, Q7]), "radius" : .5 * mm, "tangentPropagation" : true, "allowEdgeOverflow" : false});
        }
        {
            var Q0;
            Q0=makeQuery(id+"F8.boolean.opBoolean","COPY",EDGE,{"derivedFrom":makeQuery(id+"F8.opExtrude","SWEPT_EDGE",EDGE,{"disambiguationData":[OSD([sQuery(id+"F0.wireOp",EDGE,"E0.bottom"),sQuery(id+"F0.wireOp",EDGE,"E0.top"),sQuery(id+"F0.wireOp",EDGE,"E0.left"),sQuery(id+"F0.wireOp",EDGE,"E0.right"),sQuery(id+"F5.wireOp",EDGE,"E50.MirrorCS"),sQuery(id+"F5.wireOp",EDGE,"E55.MirrorCS"),sQuery(id+"F5.wireOp",EDGE,"E56.MirrorCS"),sQuery(id+"F7.wireOp",EDGE,"E59.bottom"),sQuery(id+"F7.wireOp",EDGE,"E59.left")])]})});
            var Q1;
            Q1=makeQuery(id+"F8.boolean.opBoolean","COPY",EDGE,{"derivedFrom":makeQuery(id+"F8.opExtrude","SWEPT_EDGE",EDGE,{"disambiguationData":[OSD([sQuery(id+"F7.wireOp",EDGE,"E59.top"),sQuery(id+"F7.wireOp",EDGE,"E59.left")])]})});
            var Q2;
            Q2=makeQuery(id+"F6.opExtrude","SWEPT_EDGE",EDGE,{"disambiguationData":[OSD([sQuery(id+"F5.wireOp",EDGE,"E53.MirrorCS"),sQuery(id+"F5.wireOp",EDGE,"E55.MirrorCS")])]});
            var Q3;
            Q3=makeQuery(id+"F6.opExtrude","SWEPT_EDGE",EDGE,{"disambiguationData":[OSD([sQuery(id+"F5.wireOp",EDGE,"E53.MirrorCS"),sQuery(id+"F5.wireOp",EDGE,"E58.MirrorCS")])]});
            var Q4;
            Q4=makeQuery(id+"F1.opExtrude","SWEPT_EDGE",EDGE,{"disambiguationData":[OSD([sQuery(id+"F0.wireOp",EDGE,"E0.bottom"),sQuery(id+"F0.wireOp",EDGE,"E0.right")])]});
            var Q5;
            Q5=makeQuery(id+"F8.boolean.opBoolean","COPY",EDGE,{"derivedFrom":makeQuery(id+"F8.opExtrude","SWEPT_EDGE",EDGE,{"disambiguationData":[OSD([sQuery(id+"F0.wireOp",EDGE,"E0.bottom"),sQuery(id+"F0.wireOp",EDGE,"E0.top"),sQuery(id+"F0.wireOp",EDGE,"E0.left"),sQuery(id+"F0.wireOp",EDGE,"E0.right"),sQuery(id+"F5.wireOp",EDGE,"E50.MirrorCS"),sQuery(id+"F5.wireOp",EDGE,"E55.MirrorCS"),sQuery(id+"F5.wireOp",EDGE,"E56.MirrorCS"),sQuery(id+"F7.wireOp",EDGE,"E59.bottom"),sQuery(id+"F7.wireOp",EDGE,"E59.right")])]})});
            var Q6;
            Q6=makeQuery(id+"F8.boolean.opBoolean","COPY",EDGE,{"derivedFrom":makeQuery(id+"F8.opExtrude","SWEPT_EDGE",EDGE,{"disambiguationData":[OSD([sQuery(id+"F7.wireOp",EDGE,"E59.top"),sQuery(id+"F7.wireOp",EDGE,"E59.right")])]})});
            var Q7;
            Q7=makeQuery(id+"F6.opExtrude","SWEPT_EDGE",EDGE,{"disambiguationData":[OSD([sQuery(id+"F5.wireOp",EDGE,"E39.MirrorCS"),sQuery(id+"F5.wireOp",EDGE,"E50.MirrorCS")])]});
            var Q8;
            Q8=makeQuery(id+"F6.opExtrude","SWEPT_EDGE",EDGE,{"disambiguationData":[OSD([sQuery(id+"F5.wireOp",EDGE,"E39.MirrorCS"),sQuery(id+"F5.wireOp",EDGE,"E48.MirrorCS")])]});
            var Q9;
            Q9=makeQuery(id+"F1.opExtrude","SWEPT_EDGE",EDGE,{"disambiguationData":[OSD([sQuery(id+"F0.wireOp",EDGE,"E0.bottom"),sQuery(id+"F0.wireOp",EDGE,"E0.left")])]});
            var Q10;
            Q10=makeQuery(id+"F6.opExtrude","SWEPT_EDGE",EDGE,{"disambiguationData":[OSD([sQuery(id+"F5.wireOp",EDGE,"E30.top"),sQuery(id+"F5.wireOp",EDGE,"E30.right")])]});
            var Q11;
            Q11=makeQuery(id+"F1.opExtrude","SWEPT_EDGE",EDGE,{"disambiguationData":[OSD([sQuery(id+"F0.wireOp",EDGE,"E0.top"),sQuery(id+"F0.wireOp",EDGE,"E0.left")])]});
            var Q12;
            Q12=makeQuery(id+"F6.opExtrude","SWEPT_EDGE",EDGE,{"disambiguationData":[OSD([sQuery(id+"F5.wireOp",EDGE,"E30.bottom"),sQuery(id+"F5.wireOp",EDGE,"E30.right")])]});
            var Q13;
            Q13=makeQuery(id+"F8.boolean.opBoolean","COPY",EDGE,{"derivedFrom":makeQuery(id+"F8.opExtrude","SWEPT_EDGE",EDGE,{"disambiguationData":[OSD([sQuery(id+"F7.wireOp",EDGE,"E62.MirrorCS"),sQuery(id+"F7.wireOp",EDGE,"E64.MirrorCS")])]})});
            var Q14;
            Q14=makeQuery(id+"F8.boolean.opBoolean","COPY",EDGE,{"derivedFrom":makeQuery(id+"F8.opExtrude","SWEPT_EDGE",EDGE,{"disambiguationData":[OSD([sQuery(id+"F0.wireOp",EDGE,"E0.bottom"),sQuery(id+"F0.wireOp",EDGE,"E0.top"),sQuery(id+"F0.wireOp",EDGE,"E0.left"),sQuery(id+"F0.wireOp",EDGE,"E0.right"),sQuery(id+"F5.wireOp",EDGE,"E12.top"),sQuery(id+"F5.wireOp",EDGE,"E22.top"),sQuery(id+"F5.wireOp",EDGE,"E30.bottom"),sQuery(id+"F7.wireOp",EDGE,"E63.MirrorCS"),sQuery(id+"F7.wireOp",EDGE,"E64.MirrorCS")])]})});
            var Q15;
            Q15=makeQuery(id+"F8.boolean.opBoolean","COPY",EDGE,{"derivedFrom":makeQuery(id+"F8.opExtrude","SWEPT_EDGE",EDGE,{"disambiguationData":[OSD([sQuery(id+"F7.wireOp",EDGE,"E62.MirrorCS"),sQuery(id+"F7.wireOp",EDGE,"E65.MirrorCS")])]})});
            var Q16;
            Q16=makeQuery(id+"F8.boolean.opBoolean","COPY",EDGE,{"derivedFrom":makeQuery(id+"F8.opExtrude","SWEPT_EDGE",EDGE,{"disambiguationData":[OSD([sQuery(id+"F0.wireOp",EDGE,"E0.bottom"),sQuery(id+"F0.wireOp",EDGE,"E0.top"),sQuery(id+"F0.wireOp",EDGE,"E0.left"),sQuery(id+"F0.wireOp",EDGE,"E0.right"),sQuery(id+"F5.wireOp",EDGE,"E12.top"),sQuery(id+"F5.wireOp",EDGE,"E22.top"),sQuery(id+"F5.wireOp",EDGE,"E30.bottom"),sQuery(id+"F7.wireOp",EDGE,"E63.MirrorCS"),sQuery(id+"F7.wireOp",EDGE,"E65.MirrorCS")])]})});
            var Q17;
            Q17=makeQuery(id+"F6.opExtrude","SWEPT_EDGE",EDGE,{"disambiguationData":[OSD([sQuery(id+"F5.wireOp",EDGE,"E22.bottom"),sQuery(id+"F5.wireOp",EDGE,"E22.right")])]});
            var Q18;
            Q18=makeQuery(id+"F6.opExtrude","SWEPT_EDGE",EDGE,{"disambiguationData":[OSD([sQuery(id+"F5.wireOp",EDGE,"E22.top"),sQuery(id+"F5.wireOp",EDGE,"E22.right")])]});
            var Q19;
            Q19=makeQuery(id+"F1.opExtrude","SWEPT_EDGE",EDGE,{"disambiguationData":[OSD([sQuery(id+"F0.wireOp",EDGE,"E0.top"),sQuery(id+"F0.wireOp",EDGE,"E0.right")])]});
            var Q20;
            Q20=makeQuery(id+"F14.opExtrude","SWEPT_EDGE",EDGE,{"disambiguationData":[OSD([sQuery(id+"F13.wireOp",EDGE,"E76.top"),sQuery(id+"F13.wireOp",EDGE,"E76.left")])]});
            var Q21;
            Q21=makeQuery(id+"F14.opExtrude","SWEPT_EDGE",EDGE,{"disambiguationData":[OSD([sQuery(id+"F13.wireOp",EDGE,"E76.top"),sQuery(id+"F13.wireOp",EDGE,"E76.right")])]});
            var Q22;
            Q22=makeQuery(id+"F14.opExtrude","SWEPT_EDGE",EDGE,{"disambiguationData":[OSD([sQuery(id+"F13.wireOp",EDGE,"E76.bottom"),sQuery(id+"F13.wireOp",EDGE,"E76.left")])]});
            var Q23;
            Q23=makeQuery(id+"F14.opExtrude","SWEPT_EDGE",EDGE,{"disambiguationData":[OSD([sQuery(id+"F13.wireOp",EDGE,"E76.bottom"),sQuery(id+"F13.wireOp",EDGE,"E76.right")])]});
            fillet(context, id + "F17", {"entities" : qUnion([Q0, Q1, Q2, Q3, Q4, Q5, Q6, Q7, Q8, Q9, Q10, Q11, Q12, Q13, Q14, Q15, Q16, Q17, Q18, Q19, Q20, Q21, Q22, Q23]), "radius" : 5 * mm, "tangentPropagation" : true, "allowEdgeOverflow" : false});
        }
        {
            var Q0;
            {var subQ0=sQuery(id+"F0.wireOp",EDGE,"E0.right");var subQ1=sQuery(id+"F0.wireOp",EDGE,"E0.left");var subQ2=sQuery(id+"F0.wireOp",EDGE,"E0.top");var subQ3=sQuery(id+"F0.wireOp",EDGE,"E0.bottom");Q0=makeQuery(id+"F14.boolean.opBoolean","MERGE",FACE,{"derivedFrom":[makeQuery(id+"F6.boolean.opBoolean","MERGE",FACE,{"derivedFrom":[makeQuery(id+"F1.opExtrude","CAP_FACE",FACE,{"disambiguationData":[OSD([subQ3,subQ2,subQ1,subQ0])],"isStart":false}),makeQuery(id+"F6.opExtrude","CAP_FACE",FACE,{"disambiguationData":[OSD([subQ3,subQ2,subQ1,subQ0]),OD(0.0)],"isStart":false}),makeQuery(id+"F6.opExtrude","CAP_FACE",FACE,{"disambiguationData":[OSD([subQ3,subQ2,subQ1,subQ0]),OD(1.0)],"isStart":false})]}),makeQuery(id+"F14.opExtrude","CAP_FACE",FACE,{"disambiguationData":[OSD([subQ3,subQ2,subQ1,subQ0])],"isStart":false})]});}
            var sketch = newSketch(context, id + "F18", { "sketchPlane" : qUnion([Q0])});
            skCircle(sketch, "E83", {"center": v(-34.98, 35) * mm, "radius": 1.88 * mm});
            skCircle(sketch, "E84", {"center": v(34.98, 35) * mm, "radius": 1.88 * mm});
            skLineSegment(sketch, "E85", {"start": v(-34.98, 35) * mm, "end": v(34.98, 35) * mm, "construction": true});
            skLineSegment(sketch, "E86", {"start": v(0, 45) * mm, "end": v(0, 35) * mm, "construction": true});
            skSolve(sketch);
        }
        {
            var Q0;
            Q0 = qSketchRegion(id + "F18", true);
            extrude(context, id + "F19", {"entities" : qUnion([Q0]), "operationType" : NewBodyOperationType.REMOVE, "endBound" : BoundingType.THROUGH_ALL, "oppositeDirection" : true, "depth" : 25 * mm, "offsetDistance" : 25 * mm});
        }
    });
